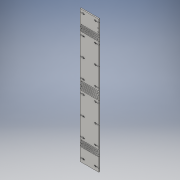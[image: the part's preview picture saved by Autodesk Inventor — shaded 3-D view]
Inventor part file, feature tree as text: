
AUTODESK INVENTOR PART (.ipt)
format: ipt  version: 2016 (Build 200138000, 138)  size: 492,032 bytes
history: native  units: in
note: dims shown in document units (in); Inventor stores cm internally (conversion verified against a paired STEP export)
features: extrude x2, sketch x2
ambient origin geometry x8: Origin, YZ Plane, XZ Plane, XY Plane, X Axis, Y Axis, Z Axis, Center Point
bodies: Solid1 (feature_tree)
feature tree (4):
  extrude  "Extrusion1"  Depth=0.1in
  extrude  "Extrusion2"  Depth=2.7414in
  sketch  "Sketch1"  dims[d34=0.427in d66=0.1in]
  sketch  "Sketch2"  dims[d94=2.7414in d95=2.7414in d109=0.305in d125=2.741in d127=0.6074in d128=0.6074in d130=0.6074in d162=0.942in d166=2.0in d167=2.0in d179=20.1074in d180=0.18in d181=0.0in d184=1.5in d188=1.5in d190=2.0in d191=0.9422in d192=2.84in d193=2.84in d194=2.84in d195=1.5in d197=0.1178in d198=0.1178in d199=0.1178in d200=2.2356in d201=1.5in d206=0.192in d207=2.84in d211=2.84in d212=2.84in d213=2.84in d214=2.84in d216=2.84in d217=2.84in d218=2.84in d219=2.84in d220=2.84in d221=2.84in d222=2.84in d223=0.427in d224=0.192in d228=2.84in d233=0.1in d234=0.1in d235=0.192in d236=0.1in d237=0.427in d238=0.192in d239=0.1in d240=0.427in d241=0.1923in d242=0.1004in d243=0.427in d244=0.1923in d245=0.1004in d246=0.427in d247=0.1004in d248=0.1923in d251=0.1004in d252=0.1923in d253=0.1923in d254=0.1004in d255=0.1923in d256=0.1004in d257=0.427in d258=0.1923in d259=0.1004in d260=0.427in d261=2.84in d262=0.1004in d263=0.1923in d264=0.1923in d265=0.427in d266=0.1in d267=0.192in d268=0.427in d269=0.192in d270=0.1in d271=0.427in d272=0.1in d273=0.192in d274=0.192in d275=0.1in d276=0.427in d277=0.192in d278=0.1in d279=0.427in d280=2.84in d281=2.84in d282=2.84in d283=2.84in d284=2.741in d285=2.741in d286=0.428in d287=0.062in d288=90.0deg d289=0.1in d290=0.192in d291=0.1in d292=0.062in d293=1.483in d294=0.252in d295=0.252in d296=0.12in d297=0.12in d298=0.1in d299=0.1in d300=1.0in d301=0.0in]
